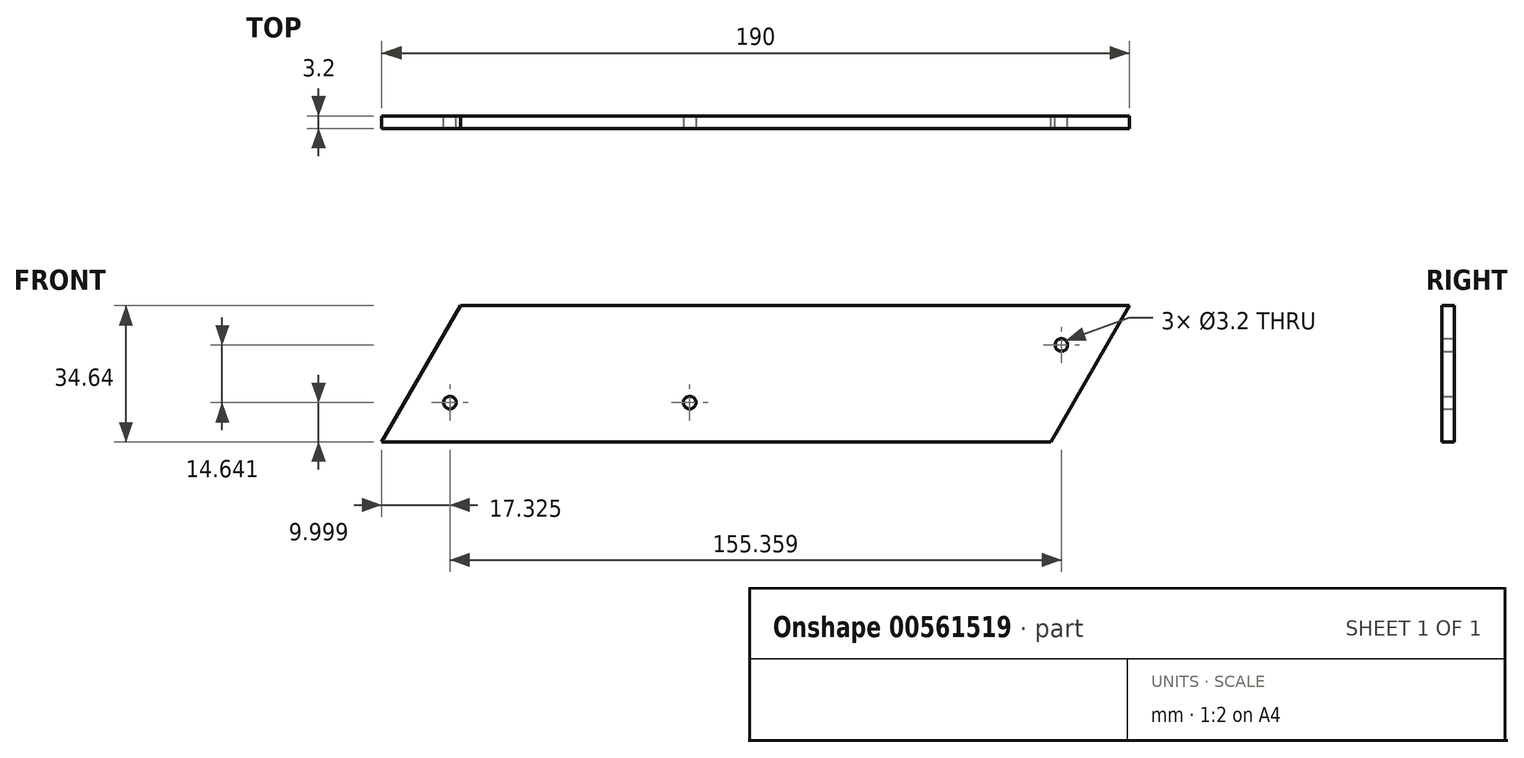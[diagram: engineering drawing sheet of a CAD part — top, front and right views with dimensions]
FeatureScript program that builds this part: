
annotation { "Feature Type Name" : "Feature", "Feature Type Description" : "" }
export const myFeature = defineFeature(function(context is Context, id is Id, definition is map)
    precondition{}
    {
        {
            var Q0;
            Q0=qCreatedBy(makeId("Front.planeOp"),FACE);
            var sketch = newSketch(context, id + "F0", { "sketchPlane" : qUnion([Q0])});
            skLineSegment(sketch, "E0.bottom", {"start": v(103.12, 13) * mm, "end": v(-66.88, 13) * mm});
            skPoint(sketch, "E0.middle", {"position": v(-66.88, 13) * mm});
            skLineSegment(sketch, "E1", {"start": v(103.13, 13) * mm, "end": v(83.12, -21.65) * mm});
            skLineSegment(sketch, "E2", {"start": v(-66.88, 13) * mm, "end": v(-86.88, -21.65) * mm});
            skLineSegment(sketch, "E3", {"start": v(-86.88, -21.65) * mm, "end": v(83.12, -21.65) * mm});
            skLineSegment(sketch, "E4", {"start": v(-66.88, 13) * mm, "end": v(103.12, 13) * mm});
            skCircle(sketch, "E5", {"center": v(-69.55, -11.65) * mm, "radius": 1.6 * mm});
            skCircle(sketch, "E6.MirrorC", {"center": v(85.8, 3) * mm, "radius": 1.6 * mm});
            skSolve(sketch);
        }
        {
            var Q0;
            Q0=qSketchRegion(id+"F0",true);
            extrude(context, id + "F1", {"entities" : qUnion([Q0]), "depth" : 3.2 * mm, "offsetDistance" : 25 * mm});
        }
        {
            var Q0;
            Q0=makeQuery(id+"F1.opExtrude","CAP_FACE",FACE,{"disambiguationData":[OSD([sQuery(id+"F0.wireOp",EDGE,"E1"),sQuery(id+"F0.wireOp",EDGE,"E2"),sQuery(id+"F0.wireOp",EDGE,"E3"),sQuery(id+"F0.wireOp",EDGE,"E4"),sQuery(id+"F0.wireOp",EDGE,"E5"),sQuery(id+"F0.wireOp",EDGE,"E6.MirrorC")])],"isStart":false});
            var sketch = newSketch(context, id + "F2", { "sketchPlane" : qUnion([Q0])});
            skCircle(sketch, "E7", {"center": v(-8.61, -11.65) * mm, "radius": 1.6 * mm});
            skSolve(sketch);
        }
        {
            var Q0;
            Q0 = qSketchRegion(id + "F2", true);
            extrude(context, id + "F3", {"entities" : qUnion([Q0]), "operationType" : NewBodyOperationType.REMOVE, "oppositeDirection" : true, "depth" : 6 * mm, "offsetDistance" : 25 * mm});
        }
    });
